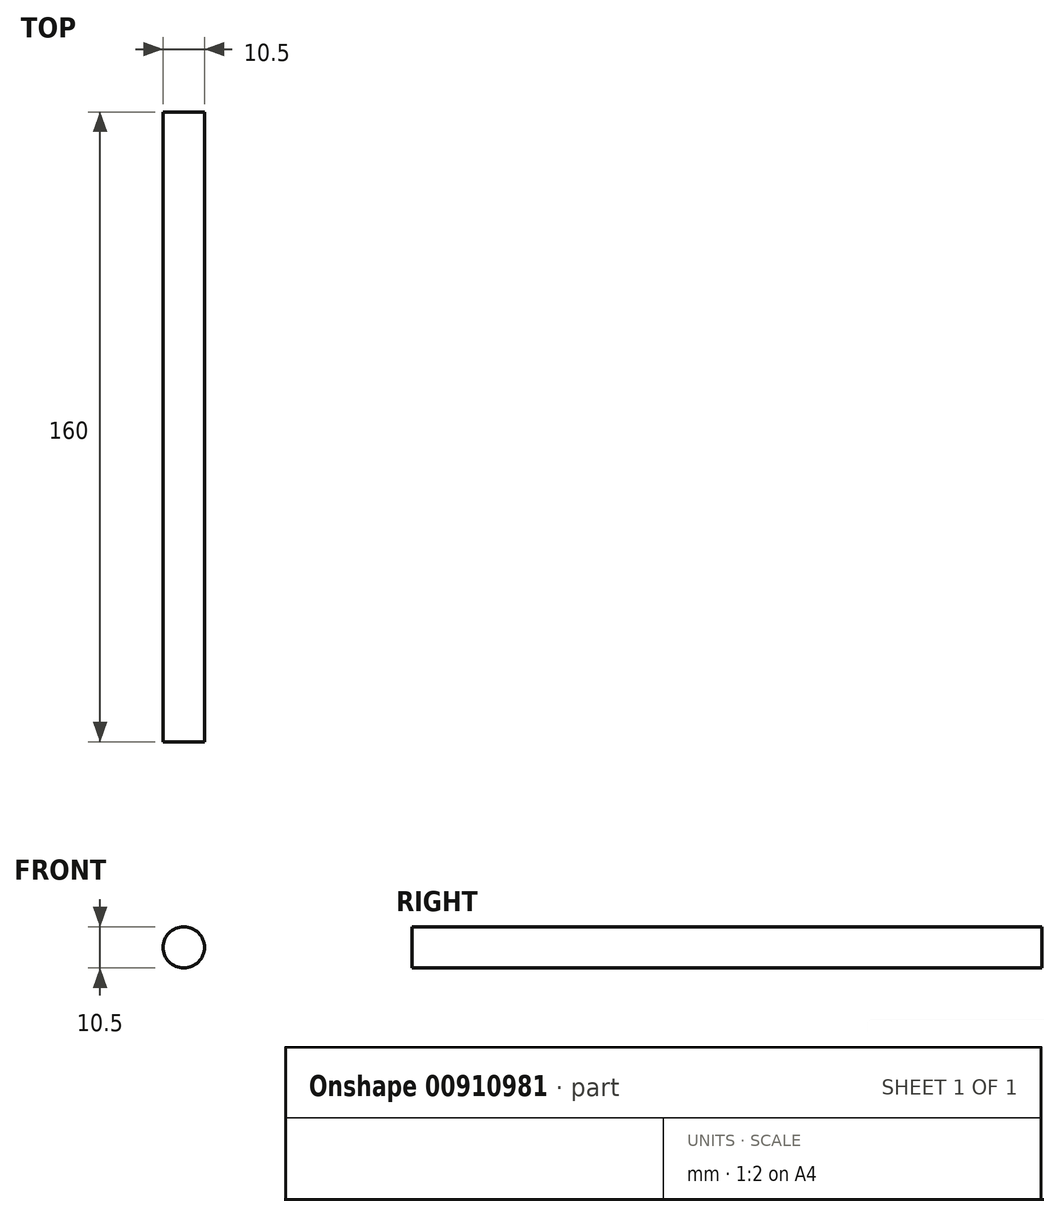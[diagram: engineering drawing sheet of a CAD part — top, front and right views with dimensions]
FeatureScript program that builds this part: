
annotation { "Feature Type Name" : "Feature", "Feature Type Description" : "" }
export const myFeature = defineFeature(function(context is Context, id is Id, definition is map)
    precondition{}
    {
        {
            var Q0;
            Q0=qCreatedBy(makeId("Front.planeOp"),FACE);
            var sketch = newSketch(context, id + "F0", { "sketchPlane" : qUnion([Q0])});
            skCircle(sketch, "E0", {"center": v(0, 0) * mm, "radius": 5.25 * mm});
            skSolve(sketch);
        }
        {
            var Q0;
            Q0=makeQuery(id+"F0.imprint","IMPRINT",FACE,{"disambiguationData":[TD([[makeQuery(id+"F0.imprint","IMPRINT",EDGE,{"derivedFrom":sQuery(id+"F0.wireOp",EDGE,"E0")}),1.0]])]});
            extrude(context, id + "F1", {"entities" : qUnion([Q0]), "depth" : 110 * mm, "offsetDistance" : 25 * mm});
        }
        {
            var Q0;
            Q0=makeQuery(id+"F1.opExtrude","CAP_FACE",FACE,{"disambiguationData":[OSD([sQuery(id+"F0.wireOp",EDGE,"E0")])],"isStart":false});
            extrude(context, id + "F2", {"entities" : qUnion([Q0]), "operationType" : NewBodyOperationType.ADD, "depth" : 100 * mm, "offsetDistance" : 25 * mm});
        }
        {
            var Q0;
            Q0=makeQuery(id+"F2.opExtrude","CAP_FACE",FACE,{"disambiguationData":[OSD([sQuery(id+"F0.wireOp",EDGE,"E0")])],"isStart":false});
            extrude(context, id + "F3", {"entities" : qUnion([Q0]), "operationType" : NewBodyOperationType.REMOVE, "oppositeDirection" : true, "depth" : 50 * mm, "offsetDistance" : 25 * mm});
        }
    });
